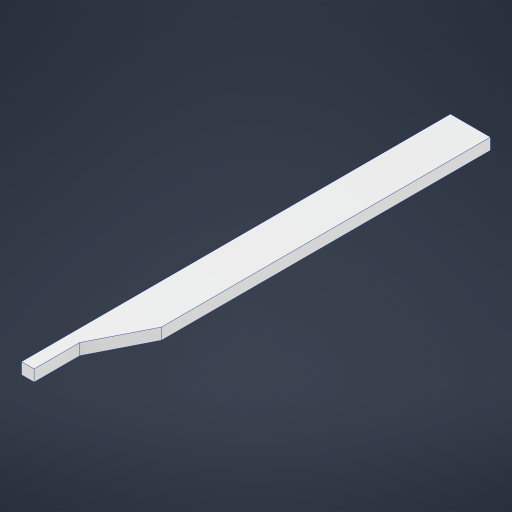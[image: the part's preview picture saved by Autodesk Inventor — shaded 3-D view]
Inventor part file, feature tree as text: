
AUTODESK INVENTOR PART (.ipt)
format: ipt  version: 2024 (Build 280153000, 153)  size: 203,776 bytes
history: native  units: mm
features: extrude x3, sketch x3
ambient origin geometry x8: Origin, YZ Plane, XZ Plane, XY Plane, X Axis, Y Axis, Z Axis, Center Point
bodies: Solid1 (feature_tree)
feature tree (6):
  extrude  "Extrusion1"  Depth=750.0mm
  extrude  "Extrusion2"  Depth=20.0mm TaperAngle=0.0deg
  extrude  "Extrusion3"  Depth=22.0mm TaperAngle=0.0deg
  sketch  "Sketch1"  dims[d0=750.0mm d1=90.0mm]
  sketch  "Sketch2"  dims[d2=20.0mm d3=0.0mm d4=25.0mm d5=0.0mm]
  sketch  "Sketch3"  dims[d7=70.0mm d8=30.0mm d9=0.0mm d10=0.0mm d11=80.0mm d13=82.0mm d14=82.0mm d15=162.0mm d16=162.0mm d17=9.0mm d18=0.0mm d19=22.0mm d20=0.0mm]
